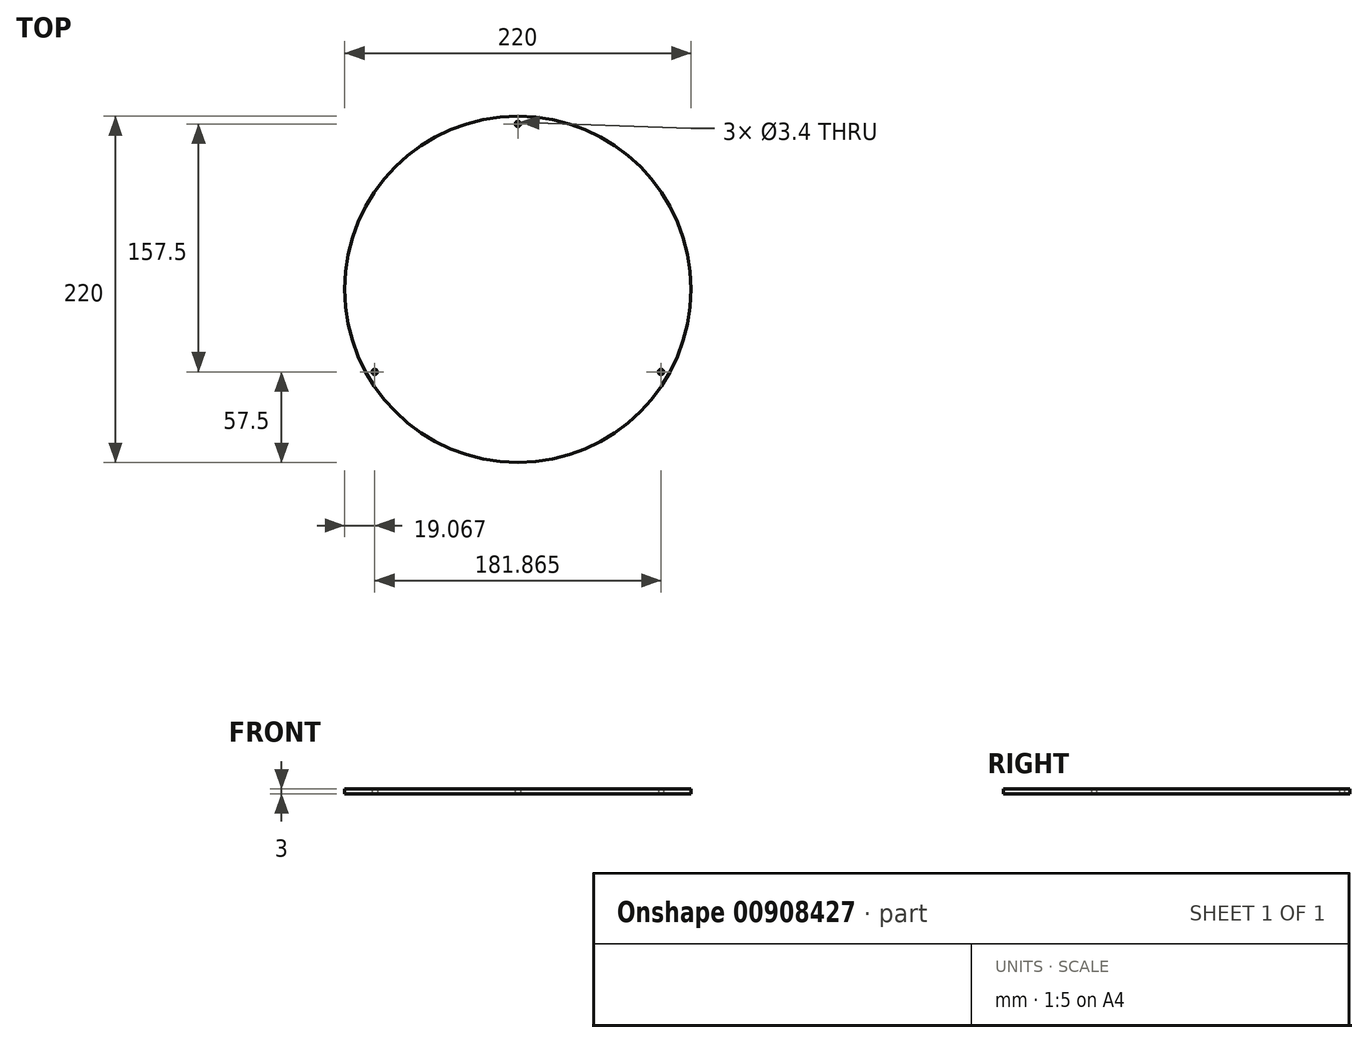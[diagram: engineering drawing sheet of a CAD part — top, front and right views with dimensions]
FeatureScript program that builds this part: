
annotation { "Feature Type Name" : "Feature", "Feature Type Description" : "" }
export const myFeature = defineFeature(function(context is Context, id is Id, definition is map)
    precondition{}
    {
        {
            var Q0;
            Q0=qCreatedBy(makeId("Top.planeOp"),FACE);
            var sketch = newSketch(context, id + "F0", { "sketchPlane" : qUnion([Q0])});
            skCircle(sketch, "E0", {"center": v(0, 0) * mm, "radius": 110 * mm});
            skCircle(sketch, "E1", {"center": v(0, 105) * mm, "radius": 1.7 * mm});
            skCircle(sketch, "E2.1.0", {"center": v(-90.93, -52.5) * mm, "radius": 1.7 * mm});
            skCircle(sketch, "E2.2.0", {"center": v(90.93, -52.5) * mm, "radius": 1.7 * mm});
            skSolve(sketch);
        }
        {
            var Q0;
            Q0=qSketchRegion(id+"F0",true);
            extrude(context, id + "F1", {"entities" : qUnion([Q0]), "depth" : 3 * mm, "offsetDistance" : 25 * mm});
        }
    });
